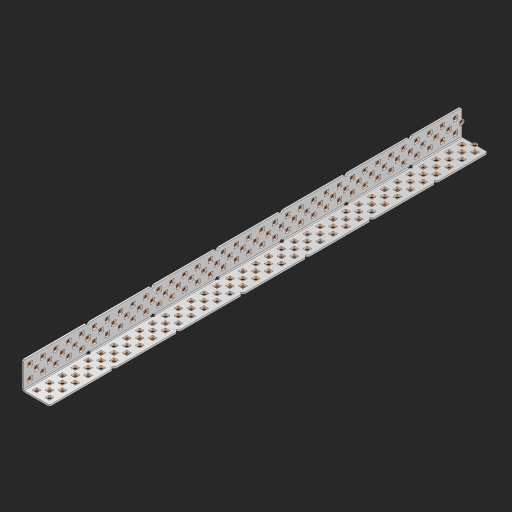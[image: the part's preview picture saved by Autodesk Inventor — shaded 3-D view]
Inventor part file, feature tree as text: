
AUTODESK INVENTOR PART (.ipt)
format: ipt  version: 2023 (Build 270158000, 158)  size: 2,186,240 bytes
history: native  units: in
note: dims shown in document units (in); Inventor stores cm internally (conversion verified against a paired STEP export)
features: other x210, extrude x202, sheet_metal_op x8, sketch x7, pattern_linear x2, mirror x1, chamfer x1
ambient origin geometry x8: Origin, YZ Plane, XZ Plane, XY Plane, X Axis, Y Axis, Z Axis, Center Point
bodies: Solid1 (feature_tree), Body (feature_tree)
feature tree (431):
  sheet_metal_op  "Flanges"
  sheet_metal_op  "Body Pattern"
  pattern_linear  "Center Pattern"  Spacing1=1.0in  [1 undecoded]
  other  "Arc Length"
  pattern_linear  "Notch Pattern"  Spacing1=0.25in  [1 undecoded]
  other  "Diagonal Plane"
  mirror  "Everything Mirrored"
  chamfer  "End Chamfer"
  sketch  "Sketch1"  dims[d0=1.0in]
  other  "Plate1"
  sketch  "Sketch2"  dims[d1=17.0in]
  other  "Plate2"
  sheet_metal_op  "Bend1"
  sheet_metal_op  "Corner1"
  sketch  "Sketch8"  dims[d2=0.0625in]
  sketch  "Sketch9"  dims[d3=0.0625in]
  other  "Srf91"
  sheet_metal_op  "Body Pattern Sketch"
  other  "Srf92"
  sketch  "Sketch13"  dims[d4=0.0312in]
  sketch  "Sketch15"  dims[d5=0.125in]
  sketch  "Sketch16"  dims[d6=0.0625in d7=1.0in d8=90.0deg d9=0.0312in d10=0.25in d11=0.0625in d12=0.0625in d49=0.182in d50=0.02in d52=0.25in d53=0.0625in d54=0.0in d55=0.172in d56=1.0in d57=0.0in d60=13.3858in d62=0.5in d63=0.7874in d65=0.5in d85=0.1473in d86=0.1782in d89=0.0625in d90=0.0in d91=0.04in d92=0.0491in d95=2.5in d96=0.04in d97=0.25in d98=45.0deg d99=0.25in d106=0.182in d107=0.02in d108=0.5in d110=0.0625in d111=0.0in d112=0.172in d113=0.5in d114=0.0in d117=0.5in d123=0.25in d125=0.25in d126=0.0491in d127=0.1473in d128=0.08in d129=0.04in d130=2.5in]
  other  "Srf786"
  other  "Srf856"
  other  "Srf857"
  other  "Srf858"
  other  "Srf859"
  other  "Srf860"
  other  "Srf861"
  other  "Srf889"
  other  "Srf890"
  other  "Srf891"
  other  "Srf1275"
  other  "Srf1276"
  other  "Srf1278"
  other  "Srf1279"
  other  "Srf1280"
  other  "Srf1281"
  other  "Srf1282"
  other  "Srf1283"
  other  "Srf1277"
  other  "Srf1285"
  other  "Srf1286"
  other  "Srf1287"
  other  "Srf1383"
  other  "Srf1384"
  other  "Srf1385"
  other  "Srf1386"
  other  "Srf1387"
  other  "Srf1388"
  other  "Srf1389"
  other  "Srf1390"
  other  "Srf1391"
  other  "Srf1392"
  other  "Srf1393"
  other  "Srf1394"
  other  "Srf1395"
  other  "Srf1396"
  other  "Srf1397"
  other  "Srf1398"
  other  "Srf1399"
  other  "Srf1400"
  other  "Srf1401"
  other  "Srf1402"
  other  "Srf1403"
  other  "Srf1404"
  other  "Srf1405"
  other  "Srf1406"
  other  "Srf1407"
  other  "Srf1408"
  other  "Srf1409"
  other  "Srf1410"
  other  "Srf1411"
  other  "Srf1412"
  other  "Srf1413"
  other  "Srf1414"
  other  "Srf1415"
  other  "Srf1416"
  other  "Srf1417"
  other  "Srf1418"
  other  "Srf1419"
  other  "Srf1420"
  other  "Srf1421"
  other  "Srf1422"
  other  "Srf1423"
  other  "Srf1424"
  other  "Srf1425"
  other  "Srf1426"
  other  "Srf1427"
  other  "Srf1428"
  other  "Srf1429"
  other  "Srf1430"
  other  "Srf1431"
  other  "Srf1432"
  other  "Srf1433"
  other  "Srf1434"
  other  "Srf1435"
  other  "Srf1436"
  other  "Srf1437"
  other  "Srf1438"
  other  "Srf1439"
  other  "Srf1440"
  other  "Srf1441"
  other  "Srf1442"
  other  "Srf1445"
  other  "Srf1446"
  other  "Srf1447"
  other  "Srf1448"
  other  "Srf1449"
  other  "Srf1450"
  other  "Srf1451"
  other  "Srf1452"
  other  "Srf1453"
  other  "Srf1454"
  other  "Srf1455"
  other  "Srf1456"
  other  "Srf1457"
  other  "Srf1458"
  other  "Srf1459"
  other  "Srf1460"
  other  "Srf1461"
  other  "Srf1462"
  other  "Srf1463"
  other  "Srf1464"
  other  "Srf1465"
  other  "Srf1466"
  other  "Srf1467"
  other  "Srf1468"
  other  "Srf1469"
  other  "Srf1470"
  other  "Srf1471"
  other  "Srf1472"
  other  "Srf1473"
  other  "Srf1474"
  other  "Srf1475"
  other  "Srf1476"
  other  "Srf1477"
  other  "Srf1478"
  other  "Srf1479"
  other  "Srf1480"
  other  "Srf1481"
  other  "Srf1482"
  other  "Srf1483"
  other  "Srf1484"
  other  "Srf1485"
  other  "Srf1486"
  other  "Srf1487"
  other  "Srf1488"
  other  "Srf1489"
  other  "Srf1490"
  other  "Srf1491"
  other  "Srf1492"
  other  "Srf1493"
  other  "Srf1494"
  other  "Srf1495"
  other  "Srf1496"
  other  "Srf1497"
  other  "Srf1498"
  other  "Srf1499"
  other  "Srf1500"
  other  "Srf1501"
  other  "Srf1502"
  other  "Srf1503"
  other  "Srf1504"
  other  "Srf1505"
  other  "Srf1506"
  other  "Srf1507"
  other  "Srf1508"
  other  "Srf1509"
  other  "Srf1510"
  other  "Srf1511"
  other  "Srf1512"
  other  "Srf1513"
  other  "Srf1514"
  other  "Srf1515"
  other  "Srf1516"
  other  "Srf1517"
  other  "Srf1518"
  other  "Srf1519"
  other  "Srf1520"
  other  "Srf1521"
  other  "Srf1522"
  other  "Srf1523"
  other  "Srf1524"
  other  "Srf1525"
  other  "Srf1526"
  other  "Srf1527"
  other  "Srf1528"
  other  "Srf1529"
  other  "Srf1530"
  other  "Srf1531"
  other  "Srf1532"
  other  "Srf1533"
  other  "Srf1534"
  other  "Srf1537"
  other  "Srf1538"
  other  "Srf1539"
  other  "Srf1540"
  other  "Srf1541"
  other  "Srf1542"
  other  "Srf1543"
  other  "Srf1544"
  other  "Srf1545"
  other  "Srf1546"
  other  "Srf1547"
  other  "Srf1548"
  other  "Srf1549"
  other  "Srf1550"
  other  "Srf1551"
  other  "Srf1552"
  other  "Srf1553"
  other  "Srf1554"
  other  "Srf1555"
  other  "Srf1556"
  other  "Srf1557"
  other  "Srf1558"
  other  "Srf1559"
  other  "Srf1560"
  other  "Srf1561"
  other  "Srf1562"
  other  "Srf1563"
  other  "Srf1564"
  other  "Srf1565"
  other  "Srf1566"
  sheet_metal_op  "Body Stamp"
  sheet_metal_op  "Body Circle"
  other  "Center Stamp"
  other  "Center Circle"
  sheet_metal_op  "Notch"
  extrude  "ExtrusionSrf92"  Depth=0.0625in
  extrude  "ExtrusionSrf856"  Depth=0.0625in
  extrude  "ExtrusionSrf857"  Depth=0.182in
  extrude  "ExtrusionSrf858"  Depth=0.02in
  extrude  "ExtrusionSrf859"  Depth=0.25in
  extrude  "ExtrusionSrf860"  Depth=0.0625in
  extrude  "ExtrusionSrf861"  TaperAngle=0.0deg  [1 undecoded]
  extrude  "ExtrusionSrf889"  Depth=2.5in
  extrude  "ExtrusionSrf890"  Depth=1.0in TaperAngle=0.0deg
  extrude  "ExtrusionSrf891"  Depth=2.5in
  extrude  "ExtrusionSrf1275"  Depth=0.5in
  extrude  "ExtrusionSrf1276"  Depth=2.5in
  extrude  "ExtrusionSrf1277"  Depth=2.5in
  extrude  "ExtrusionSrf1278"  Depth=0.0625in
  extrude  "ExtrusionSrf1279"  Depth=2.5in TaperAngle=0.0deg
  extrude  "ExtrusionSrf1280"  Depth=2.5in
  extrude  "ExtrusionSrf1281"  Depth=0.25in TaperAngle=45.0deg
  extrude  "ExtrusionSrf1282"  Depth=0.25in
  extrude  "ExtrusionSrf1345"  Depth=0.182in
  extrude  "ExtrusionSrf1346"  Depth=0.02in
  extrude  "ExtrusionSrf1347"  Depth=0.5in
  extrude  "ExtrusionSrf1348"  Depth=0.0625in
  extrude  "ExtrusionSrf1383"  TaperAngle=0.0deg  [1 undecoded]
  extrude  "ExtrusionSrf1384"  Depth=2.5in
  extrude  "ExtrusionSrf1385"  Depth=0.5in TaperAngle=0.0deg
  extrude  "ExtrusionSrf1386"  Depth=0.5in
  extrude  "ExtrusionSrf1387"  Depth=0.25in
  extrude  "ExtrusionSrf1388"  Depth=0.25in
  extrude  "ExtrusionSrf1389"  Depth=2.5in
  extrude  "ExtrusionSrf1390"  Depth=2.5in
  extrude  "ExtrusionSrf1391"  Depth=2.5in
  extrude  "ExtrusionSrf1392"  Depth=2.5in
  extrude  "ExtrusionSrf1393"  Depth=2.5in
  extrude  "ExtrusionSrf1394"  [1 undecoded]
  extrude  "ExtrusionSrf1395"  [1 undecoded]
  extrude  "ExtrusionSrf1396"  [1 undecoded]
  extrude  "ExtrusionSrf1397"  [1 undecoded]
  extrude  "ExtrusionSrf1398"  [1 undecoded]
  extrude  "ExtrusionSrf1399"  [1 undecoded]
  extrude  "ExtrusionSrf1400"  [1 undecoded]
  extrude  "ExtrusionSrf1401"  [1 undecoded]
  extrude  "ExtrusionSrf1402"  [1 undecoded]
  extrude  "ExtrusionSrf1403"  [1 undecoded]
  extrude  "ExtrusionSrf1404"  [1 undecoded]
  extrude  "ExtrusionSrf1405"  [1 undecoded]
  extrude  "ExtrusionSrf1406"  [1 undecoded]
  extrude  "ExtrusionSrf1407"  [1 undecoded]
  extrude  "ExtrusionSrf1408"  [1 undecoded]
  extrude  "ExtrusionSrf1409"  [1 undecoded]
  extrude  "ExtrusionSrf1410"  [1 undecoded]
  extrude  "ExtrusionSrf1411"  [1 undecoded]
  extrude  "ExtrusionSrf1412"  [1 undecoded]
  extrude  "ExtrusionSrf1413"  [1 undecoded]
  extrude  "ExtrusionSrf1414"  [1 undecoded]
  extrude  "ExtrusionSrf1415"  [1 undecoded]
  extrude  "ExtrusionSrf1416"  [1 undecoded]
  extrude  "ExtrusionSrf1417"  [1 undecoded]
  extrude  "ExtrusionSrf1418"  [1 undecoded]
  extrude  "ExtrusionSrf1419"  [1 undecoded]
  extrude  "ExtrusionSrf1420"  [1 undecoded]
  extrude  "ExtrusionSrf1421"  [1 undecoded]
  extrude  "ExtrusionSrf1422"  [1 undecoded]
  extrude  "ExtrusionSrf1423"  [1 undecoded]
  extrude  "ExtrusionSrf1424"  [1 undecoded]
  extrude  "ExtrusionSrf1425"  [1 undecoded]
  extrude  "ExtrusionSrf1426"  [1 undecoded]
  extrude  "ExtrusionSrf1427"  [1 undecoded]
  extrude  "ExtrusionSrf1428"  [1 undecoded]
  extrude  "ExtrusionSrf1429"  [1 undecoded]
  extrude  "ExtrusionSrf1430"  [1 undecoded]
  extrude  "ExtrusionSrf1431"  [1 undecoded]
  extrude  "ExtrusionSrf1432"  [1 undecoded]
  extrude  "ExtrusionSrf1433"  [1 undecoded]
  extrude  "ExtrusionSrf1434"  [1 undecoded]
  extrude  "ExtrusionSrf1435"  [1 undecoded]
  extrude  "ExtrusionSrf1436"  [1 undecoded]
  extrude  "ExtrusionSrf1437"  [1 undecoded]
  extrude  "ExtrusionSrf1438"  [1 undecoded]
  extrude  "ExtrusionSrf1439"  [1 undecoded]
  extrude  "ExtrusionSrf1440"  [1 undecoded]
  extrude  "ExtrusionSrf1441"  [1 undecoded]
  extrude  "ExtrusionSrf1442"  [1 undecoded]
  extrude  "ExtrusionSrf1445"  [1 undecoded]
  extrude  "ExtrusionSrf1446"  [1 undecoded]
  extrude  "ExtrusionSrf1447"  [1 undecoded]
  extrude  "ExtrusionSrf1448"  [1 undecoded]
  extrude  "ExtrusionSrf1449"  [1 undecoded]
  extrude  "ExtrusionSrf1450"  [1 undecoded]
  extrude  "ExtrusionSrf1451"  [1 undecoded]
  extrude  "ExtrusionSrf1452"  [1 undecoded]
  extrude  "ExtrusionSrf1453"  [1 undecoded]
  extrude  "ExtrusionSrf1454"  [1 undecoded]
  extrude  "ExtrusionSrf1455"  [1 undecoded]
  extrude  "ExtrusionSrf1456"  [1 undecoded]
  extrude  "ExtrusionSrf1457"  [1 undecoded]
  extrude  "ExtrusionSrf1458"  [1 undecoded]
  extrude  "ExtrusionSrf1459"  [1 undecoded]
  extrude  "ExtrusionSrf1460"  [1 undecoded]
  extrude  "ExtrusionSrf1461"  [1 undecoded]
  extrude  "ExtrusionSrf1462"  [1 undecoded]
  extrude  "ExtrusionSrf1463"  [1 undecoded]
  extrude  "ExtrusionSrf1464"  [1 undecoded]
  extrude  "ExtrusionSrf1465"  [1 undecoded]
  extrude  "ExtrusionSrf1466"  [1 undecoded]
  extrude  "ExtrusionSrf1467"  [1 undecoded]
  extrude  "ExtrusionSrf1468"  [1 undecoded]
  extrude  "ExtrusionSrf1469"  [1 undecoded]
  extrude  "ExtrusionSrf1470"  [1 undecoded]
  extrude  "ExtrusionSrf1471"  [1 undecoded]
  extrude  "ExtrusionSrf1472"  [1 undecoded]
  extrude  "ExtrusionSrf1473"  [1 undecoded]
  extrude  "ExtrusionSrf1474"  [1 undecoded]
  extrude  "ExtrusionSrf1475"  [1 undecoded]
  extrude  "ExtrusionSrf1476"  [1 undecoded]
  extrude  "ExtrusionSrf1477"  [1 undecoded]
  extrude  "ExtrusionSrf1478"  [1 undecoded]
  extrude  "ExtrusionSrf1479"  [1 undecoded]
  extrude  "ExtrusionSrf1480"  [1 undecoded]
  extrude  "ExtrusionSrf1481"  [1 undecoded]
  extrude  "ExtrusionSrf1482"  [1 undecoded]
  extrude  "ExtrusionSrf1483"  [1 undecoded]
  extrude  "ExtrusionSrf1484"  [1 undecoded]
  extrude  "ExtrusionSrf1485"  [1 undecoded]
  extrude  "ExtrusionSrf1486"  [1 undecoded]
  extrude  "ExtrusionSrf1487"  [1 undecoded]
  extrude  "ExtrusionSrf1488"  [1 undecoded]
  extrude  "ExtrusionSrf1489"  [1 undecoded]
  extrude  "ExtrusionSrf1490"  [1 undecoded]
  extrude  "ExtrusionSrf1491"  [1 undecoded]
  extrude  "ExtrusionSrf1492"  [1 undecoded]
  extrude  "ExtrusionSrf1493"  [1 undecoded]
  extrude  "ExtrusionSrf1494"  [1 undecoded]
  extrude  "ExtrusionSrf1495"  [1 undecoded]
  extrude  "ExtrusionSrf1496"  [1 undecoded]
  extrude  "ExtrusionSrf1497"  [1 undecoded]
  extrude  "ExtrusionSrf1498"  [1 undecoded]
  extrude  "ExtrusionSrf1499"  [1 undecoded]
  extrude  "ExtrusionSrf1500"  [1 undecoded]
  extrude  "ExtrusionSrf1501"  [1 undecoded]
  extrude  "ExtrusionSrf1502"  [1 undecoded]
  extrude  "ExtrusionSrf1503"  [1 undecoded]
  extrude  "ExtrusionSrf1504"  [1 undecoded]
  extrude  "ExtrusionSrf1505"  [1 undecoded]
  extrude  "ExtrusionSrf1506"  [1 undecoded]
  extrude  "ExtrusionSrf1507"  [1 undecoded]
  extrude  "ExtrusionSrf1508"  [1 undecoded]
  extrude  "ExtrusionSrf1509"  [1 undecoded]
  extrude  "ExtrusionSrf1510"  [1 undecoded]
  extrude  "ExtrusionSrf1511"  [1 undecoded]
  extrude  "ExtrusionSrf1512"  [1 undecoded]
  extrude  "ExtrusionSrf1513"  [1 undecoded]
  extrude  "ExtrusionSrf1514"  [1 undecoded]
  extrude  "ExtrusionSrf1515"  [1 undecoded]
  extrude  "ExtrusionSrf1516"  [1 undecoded]
  extrude  "ExtrusionSrf1517"  [1 undecoded]
  extrude  "ExtrusionSrf1518"  [1 undecoded]
  extrude  "ExtrusionSrf1519"  [1 undecoded]
  extrude  "ExtrusionSrf1520"  [1 undecoded]
  extrude  "ExtrusionSrf1521"  [1 undecoded]
  extrude  "ExtrusionSrf1522"  [1 undecoded]
  extrude  "ExtrusionSrf1523"  [1 undecoded]
  extrude  "ExtrusionSrf1524"  [1 undecoded]
  extrude  "ExtrusionSrf1525"  [1 undecoded]
  extrude  "ExtrusionSrf1526"  [1 undecoded]
  extrude  "ExtrusionSrf1527"  [1 undecoded]
  extrude  "ExtrusionSrf1528"  [1 undecoded]
  extrude  "ExtrusionSrf1529"  [1 undecoded]
  extrude  "ExtrusionSrf1530"  [1 undecoded]
  extrude  "ExtrusionSrf1531"  [1 undecoded]
  extrude  "ExtrusionSrf1532"  [1 undecoded]
  extrude  "ExtrusionSrf1533"  [1 undecoded]
  extrude  "ExtrusionSrf1534"  [1 undecoded]
  extrude  "ExtrusionSrf1537"  [1 undecoded]
  extrude  "ExtrusionSrf1538"  [1 undecoded]
  extrude  "ExtrusionSrf1539"  [1 undecoded]
  extrude  "ExtrusionSrf1540"  [1 undecoded]
  extrude  "ExtrusionSrf1541"  [1 undecoded]
  extrude  "ExtrusionSrf1542"  [1 undecoded]
  extrude  "ExtrusionSrf1543"  [1 undecoded]
  extrude  "ExtrusionSrf1544"  [1 undecoded]
  extrude  "ExtrusionSrf1545"  [1 undecoded]
  extrude  "ExtrusionSrf1546"  [1 undecoded]
  extrude  "ExtrusionSrf1547"  [1 undecoded]
  extrude  "ExtrusionSrf1548"  [1 undecoded]
  extrude  "ExtrusionSrf1549"  [1 undecoded]
  extrude  "ExtrusionSrf1550"  [1 undecoded]
  extrude  "ExtrusionSrf1551"  [1 undecoded]
  extrude  "ExtrusionSrf1552"  [1 undecoded]
  extrude  "ExtrusionSrf1553"  [1 undecoded]
  extrude  "ExtrusionSrf1554"  [1 undecoded]
  extrude  "ExtrusionSrf1555"  [1 undecoded]
  extrude  "ExtrusionSrf1556"  [1 undecoded]
  extrude  "ExtrusionSrf1557"  [1 undecoded]
  extrude  "ExtrusionSrf1558"  [1 undecoded]
  extrude  "ExtrusionSrf1559"  [1 undecoded]
  extrude  "ExtrusionSrf1560"  [1 undecoded]
  extrude  "ExtrusionSrf1561"  [1 undecoded]
  extrude  "ExtrusionSrf1562"  [1 undecoded]
  extrude  "ExtrusionSrf1563"  [1 undecoded]
  extrude  "ExtrusionSrf1564"  [1 undecoded]
  extrude  "ExtrusionSrf1565"  [1 undecoded]
  extrude  "ExtrusionSrf1566"  [1 undecoded]
note: 173 required parameter values undecoded (feature->parameter linkage not recoverable at this tier; creation-order binding heuristic only, values carry confidence <= 0.55)
